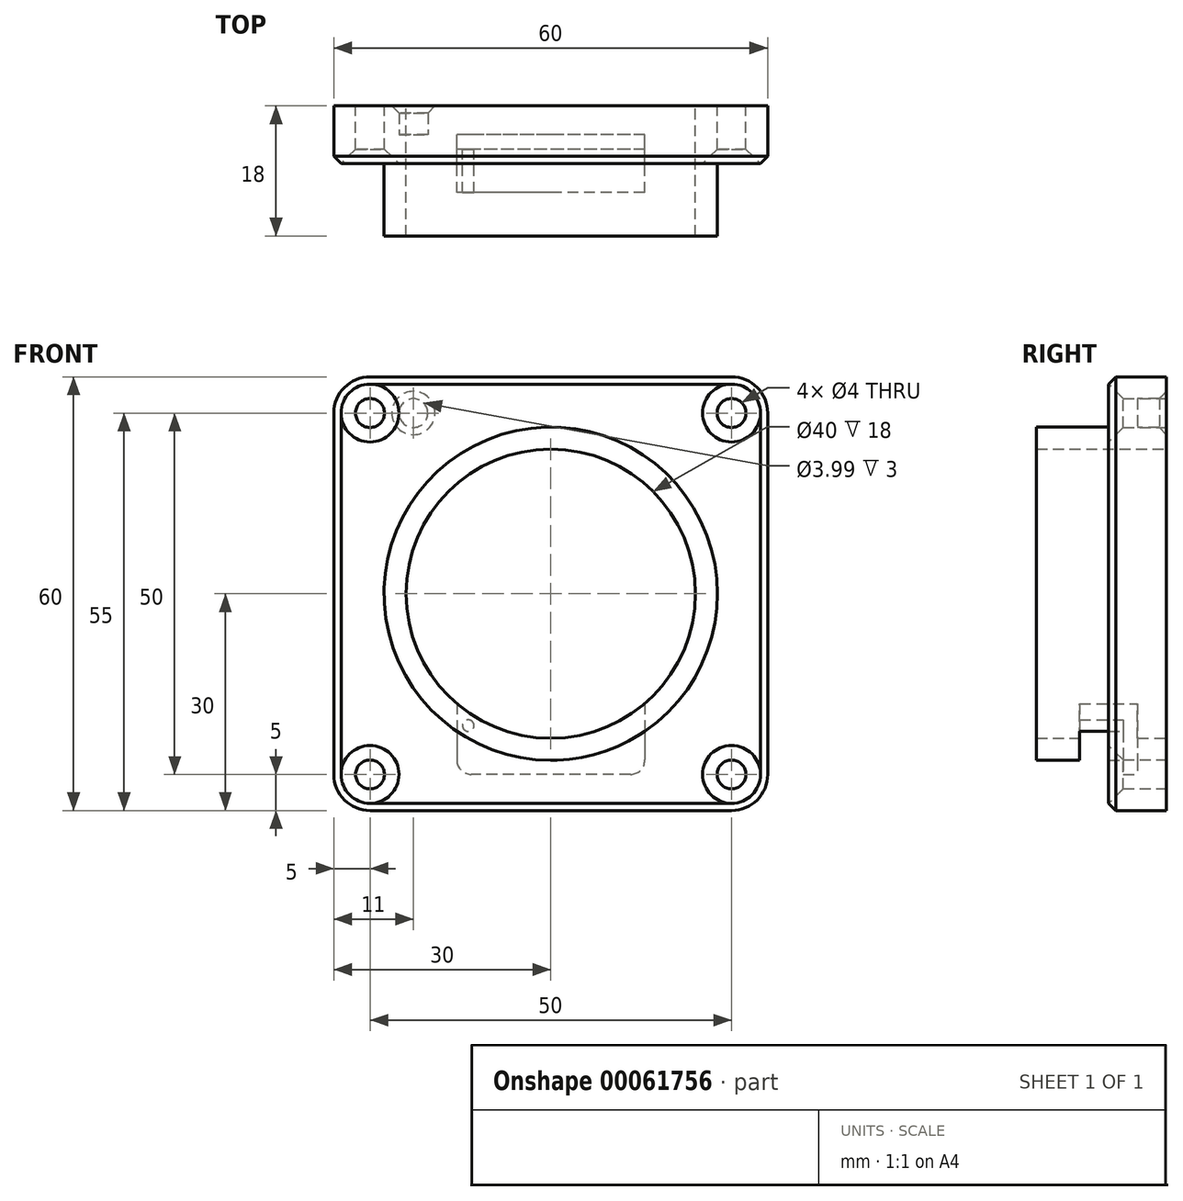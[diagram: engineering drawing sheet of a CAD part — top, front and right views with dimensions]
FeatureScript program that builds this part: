
annotation { "Feature Type Name" : "Feature", "Feature Type Description" : "" }
export const myFeature = defineFeature(function(context is Context, id is Id, definition is map)
    precondition{}
    {
        {
            var Q0;
            Q0=qCreatedBy(makeId("Front.planeOp"),FACE);
            var sketch = newSketch(context, id + "F0", { "sketchPlane" : qUnion([Q0])});
            skLineSegment(sketch, "E0.bottom", {"start": v(25, 30) * mm, "end": v(-25, 30) * mm});
            skLineSegment(sketch, "E0.top", {"start": v(25, -30) * mm, "end": v(-25, -30) * mm});
            skLineSegment(sketch, "E0.left", {"start": v(30, 25) * mm, "end": v(30, -25) * mm});
            skLineSegment(sketch, "E0.right", {"start": v(-30, 25) * mm, "end": v(-30, -25) * mm});
            skPoint(sketch, "E1", {"position": v(0, 30) * mm});
            skPoint(sketch, "E2", {"position": v(30, 0) * mm});
            skCircle(sketch, "E3", {"center": v(-25, 25) * mm, "radius": 2 * mm});
            skCircle(sketch, "E4.MirrorC", {"center": v(25, 25) * mm, "radius": 2 * mm});
            skCircle(sketch, "E5.MirrorC", {"center": v(-25, -25) * mm, "radius": 2 * mm});
            skCircle(sketch, "E6.MirrorC", {"center": v(25, -25) * mm, "radius": 2 * mm});
            skPoint(sketch, "E7.visualSharp", {"position": v(-30, 30) * mm});
            skArc(sketch, "E7.filletArc", {"start": v(-25, 30) * mm, "mid": v(-28.54, 28.54) * mm, "end": v(-30, 25) * mm});
            skPoint(sketch, "E8.visualSharp", {"position": v(30, 30) * mm});
            skArc(sketch, "E8.filletArc", {"start": v(30, 25) * mm, "mid": v(28.54, 28.54) * mm, "end": v(25, 30) * mm});
            skPoint(sketch, "E9.visualSharp", {"position": v(30, -30) * mm});
            skArc(sketch, "E9.filletArc", {"start": v(25, -30) * mm, "mid": v(28.54, -28.54) * mm, "end": v(30, -25) * mm});
            skPoint(sketch, "E10.visualSharp", {"position": v(-30, -30) * mm});
            skArc(sketch, "E10.filletArc", {"start": v(-30, -25) * mm, "mid": v(-28.54, -28.54) * mm, "end": v(-25, -30) * mm});
            skCircle(sketch, "E11", {"center": v(0, 0) * mm, "radius": 20 * mm});
            skSolve(sketch);
        }
        {
            var Q0;
            Q0=makeQuery(id+"F0.imprint","IMPRINT",FACE,{"disambiguationData":[TD([[makeQuery(id+"F0.imprint","IMPRINT",EDGE,{"derivedFrom":sQuery(id+"F0.wireOp",EDGE,"E0.bottom")}),1.0]])]});
            extrude(context, id + "F1", {"entities" : qUnion([Q0]), "depth" : 4 * mm});
        }
        {
            var Q0;
            Q0=makeQuery(id+"F1.opExtrude","CAP_FACE",FACE,{"disambiguationData":[OSD([sQuery(id+"F0.wireOp",EDGE,"E0.bottom"),sQuery(id+"F0.wireOp",EDGE,"E0.top"),sQuery(id+"F0.wireOp",EDGE,"E0.left"),sQuery(id+"F0.wireOp",EDGE,"E0.right"),sQuery(id+"F0.wireOp",EDGE,"E3"),sQuery(id+"F0.wireOp",EDGE,"E4.MirrorC"),sQuery(id+"F0.wireOp",EDGE,"E5.MirrorC"),sQuery(id+"F0.wireOp",EDGE,"E6.MirrorC"),sQuery(id+"F0.wireOp",EDGE,"E7.filletArc"),sQuery(id+"F0.wireOp",EDGE,"E8.filletArc"),sQuery(id+"F0.wireOp",EDGE,"E9.filletArc"),sQuery(id+"F0.wireOp",EDGE,"E10.filletArc"),sQuery(id+"F0.wireOp",EDGE,"74017124-3e05-427a-b8e4-af609694847d.bottom"),sQuery(id+"F0.wireOp",EDGE,"74017124-3e05-427a-b8e4-af609694847d.top"),sQuery(id+"F0.wireOp",EDGE,"74017124-3e05-427a-b8e4-af609694847d.left"),sQuery(id+"F0.wireOp",EDGE,"74017124-3e05-427a-b8e4-af609694847d.right"),sQuery(id+"F0.wireOp",EDGE,"8a5725f9-208e-47c7-ad8a-a344d27b9ad4.filletArc"),sQuery(id+"F0.wireOp",EDGE,"34e853ff-a61b-4a46-9221-9543787036cd.filletArc"),sQuery(id+"F0.wireOp",EDGE,"1b7ca9ec-e36b-44de-8ecb-2f01a231179c.filletArc"),sQuery(id+"F0.wireOp",EDGE,"5f012eeb-bb5c-4c35-9c7e-adf75f7540f9.filletArc")])],"isStart":true});
            var sketch = newSketch(context, id + "F2", { "sketchPlane" : qUnion([Q0])});
            skCircle(sketch, "E12", {"center": v(-19, 25) * mm, "radius": 2 * mm});
            skLineSegment(sketch, "E13", {"start": v(-25, 25) * mm, "end": v(25, 25) * mm, "construction": true});
            skLineSegment(sketch, "E14", {"start": v(25, 25) * mm, "end": v(25, -25) * mm, "construction": true});
            skLineSegment(sketch, "E15", {"start": v(25, -25) * mm, "end": v(-25, -25) * mm, "construction": true});
            skLineSegment(sketch, "E16", {"start": v(-25, -25) * mm, "end": v(-25, 25) * mm, "construction": true});
            skCircle(sketch, "E17.MirrorC", {"center": v(19, 25) * mm, "radius": 2 * mm});
            skCircle(sketch, "E18.MirrorC", {"center": v(19, -25) * mm, "radius": 2 * mm});
            skCircle(sketch, "E19", {"center": v(-16, -25) * mm, "radius": 2 * mm});
            skSolve(sketch);
        }
        {
            var Q0;
            Q0=makeQuery(id+"F2.imprint","IMPRINT",FACE,{"disambiguationData":[TD([[makeQuery(id+"F2.imprint","IMPRINT",EDGE,{"derivedFrom":sQuery(id+"F2.wireOp",EDGE,"E12")}),1.0]])]});
            var Q1;
            Q1=makeQuery(id+"F2.imprint","IMPRINT",FACE,{"disambiguationData":[TD([[makeQuery(id+"F2.imprint","IMPRINT",EDGE,{"derivedFrom":sQuery(id+"F2.wireOp",EDGE,"E17.MirrorC")}),-1.0]])]});
            var Q2;
            Q2=makeQuery(id+"F2.imprint","IMPRINT",FACE,{"disambiguationData":[TD([[makeQuery(id+"F2.imprint","IMPRINT",EDGE,{"derivedFrom":sQuery(id+"F2.wireOp",EDGE,"E18.MirrorC")}),1.0]])]});
            var Q3;
            Q3=makeQuery(id+"F2.imprint","IMPRINT",FACE,{"disambiguationData":[TD([[makeQuery(id+"F2.imprint","IMPRINT",EDGE,{"derivedFrom":sQuery(id+"F2.wireOp",EDGE,"E19")}),1.0]])]});
            extrude(context, id + "F3", {"entities" : qUnion([Q0, Q1, Q2, Q3]), "operationType" : NewBodyOperationType.ADD, "depth" : 4 * mm});
        }
        {
            var Q0;
            Q0=makeQuery(id+"F3.opExtrude","CAP_EDGE",EDGE,{"disambiguationData":[OSD([sQuery(id+"F2.wireOp",EDGE,"E19")])],"isStart":false});
            var Q1;
            Q1=makeQuery(id+"F3.opExtrude","CAP_EDGE",EDGE,{"disambiguationData":[OSD([sQuery(id+"F2.wireOp",EDGE,"E18.MirrorC")])],"isStart":false});
            var Q2;
            Q2=makeQuery(id+"F3.opExtrude","CAP_EDGE",EDGE,{"disambiguationData":[OSD([sQuery(id+"F2.wireOp",EDGE,"E17.MirrorC")])],"isStart":false});
            var Q3;
            Q3=makeQuery(id+"F3.opExtrude","CAP_EDGE",EDGE,{"disambiguationData":[OSD([sQuery(id+"F2.wireOp",EDGE,"E12")])],"isStart":false});
            chamfer(context, id + "F4", {"entities" : qUnion([Q0, Q1, Q2, Q3]), "width" : 1 * mm, "tangentPropagation" : true});
        }
        {
            var Q0;
            Q0=makeQuery(id+"F1.opExtrude","CAP_FACE",FACE,{"disambiguationData":[OSD([sQuery(id+"F0.wireOp",EDGE,"E0.bottom"),sQuery(id+"F0.wireOp",EDGE,"E0.top"),sQuery(id+"F0.wireOp",EDGE,"E0.left"),sQuery(id+"F0.wireOp",EDGE,"E0.right"),sQuery(id+"F0.wireOp",EDGE,"E3"),sQuery(id+"F0.wireOp",EDGE,"E4.MirrorC"),sQuery(id+"F0.wireOp",EDGE,"E5.MirrorC"),sQuery(id+"F0.wireOp",EDGE,"E6.MirrorC"),sQuery(id+"F0.wireOp",EDGE,"E7.filletArc"),sQuery(id+"F0.wireOp",EDGE,"E8.filletArc"),sQuery(id+"F0.wireOp",EDGE,"E9.filletArc"),sQuery(id+"F0.wireOp",EDGE,"E10.filletArc"),sQuery(id+"F0.wireOp",EDGE,"74017124-3e05-427a-b8e4-af609694847d.bottom"),sQuery(id+"F0.wireOp",EDGE,"74017124-3e05-427a-b8e4-af609694847d.top"),sQuery(id+"F0.wireOp",EDGE,"74017124-3e05-427a-b8e4-af609694847d.left"),sQuery(id+"F0.wireOp",EDGE,"74017124-3e05-427a-b8e4-af609694847d.right"),sQuery(id+"F0.wireOp",EDGE,"8a5725f9-208e-47c7-ad8a-a344d27b9ad4.filletArc"),sQuery(id+"F0.wireOp",EDGE,"34e853ff-a61b-4a46-9221-9543787036cd.filletArc"),sQuery(id+"F0.wireOp",EDGE,"1b7ca9ec-e36b-44de-8ecb-2f01a231179c.filletArc"),sQuery(id+"F0.wireOp",EDGE,"5f012eeb-bb5c-4c35-9c7e-adf75f7540f9.filletArc")])],"isStart":false});
            var sketch = newSketch(context, id + "F5", { "sketchPlane" : qUnion([Q0])});
            skCircle(sketch, "E20", {"center": v(0, 0) * mm, "radius": 23.05 * mm});
            skCircle(sketch, "E21", {"center": v(0, 0) * mm, "radius": 20 * mm});
            skSolve(sketch);
        }
        {
            var Q0;
            Q0=makeQuery(id+"F5.imprint","IMPRINT",FACE,{"disambiguationData":[TD([[makeQuery(id+"F5.imprint","IMPRINT",EDGE,{"derivedFrom":sQuery(id+"F5.wireOp",EDGE,"E20")}),1.0]])]});
            extrude(context, id + "F6", {"entities" : qUnion([Q0]), "operationType" : NewBodyOperationType.ADD, "depth" : 10 * mm});
        }
        {
            var Q0;
            Q0=makeQuery(id+"F1.opExtrude","CAP_FACE",FACE,{"disambiguationData":[OSD([sQuery(id+"F0.wireOp",EDGE,"E0.bottom"),sQuery(id+"F0.wireOp",EDGE,"E0.top"),sQuery(id+"F0.wireOp",EDGE,"E0.left"),sQuery(id+"F0.wireOp",EDGE,"E0.right"),sQuery(id+"F0.wireOp",EDGE,"E3"),sQuery(id+"F0.wireOp",EDGE,"E4.MirrorC"),sQuery(id+"F0.wireOp",EDGE,"E5.MirrorC"),sQuery(id+"F0.wireOp",EDGE,"E6.MirrorC"),sQuery(id+"F0.wireOp",EDGE,"E7.filletArc"),sQuery(id+"F0.wireOp",EDGE,"E8.filletArc"),sQuery(id+"F0.wireOp",EDGE,"E9.filletArc"),sQuery(id+"F0.wireOp",EDGE,"E10.filletArc"),sQuery(id+"F0.wireOp",EDGE,"E11")])],"isStart":true});
            var sketch = newSketch(context, id + "F7", { "sketchPlane" : qUnion([Q0])});
            skLineSegment(sketch, "E22.bottom", {"start": v(-13, -10) * mm, "end": v(13, -10) * mm});
            skLineSegment(sketch, "E22.top", {"start": v(-11, -25) * mm, "end": v(11, -25) * mm});
            skLineSegment(sketch, "E22.left", {"start": v(-13, -10) * mm, "end": v(-13, -23) * mm});
            skLineSegment(sketch, "E22.right", {"start": v(13, -10) * mm, "end": v(13, -23) * mm});
            skArc(sketch, "E23.0.0", {"start": v(-25, 30) * mm, "mid": v(-28.54, 28.54) * mm, "end": v(-30, 25) * mm});
            skLineSegment(sketch, "E23.0.1", {"start": v(-30, 25) * mm, "end": v(-30, -25) * mm});
            skArc(sketch, "E23.0.2", {"start": v(-30, -25) * mm, "mid": v(-28.54, -28.54) * mm, "end": v(-25, -30) * mm});
            skLineSegment(sketch, "E23.0.3", {"start": v(-25, -30) * mm, "end": v(25, -30) * mm});
            skArc(sketch, "E23.0.4", {"start": v(25, -30) * mm, "mid": v(28.54, -28.54) * mm, "end": v(30, -25) * mm});
            skLineSegment(sketch, "E23.0.5", {"start": v(30, -25) * mm, "end": v(30, 25) * mm});
            skArc(sketch, "E23.0.6", {"start": v(30, 25) * mm, "mid": v(28.54, 28.54) * mm, "end": v(25, 30) * mm});
            skLineSegment(sketch, "E23.0.7", {"start": v(25, 30) * mm, "end": v(-25, 30) * mm});
            skLineSegment(sketch, "E24", {"start": v(-25, -25) * mm, "end": v(25, -25) * mm, "construction": true});
            skPoint(sketch, "E25", {"position": v(0, -10) * mm});
            skPoint(sketch, "E26.visualSharp", {"position": v(-13, -25) * mm});
            skArc(sketch, "E26.filletArc", {"start": v(-13, -23) * mm, "mid": v(-12.41, -24.41) * mm, "end": v(-11, -25) * mm});
            skPoint(sketch, "E27.visualSharp", {"position": v(13, -25) * mm});
            skArc(sketch, "E27.filletArc", {"start": v(11, -25) * mm, "mid": v(12.41, -24.41) * mm, "end": v(13, -23) * mm});
            skSolve(sketch);
        }
        {
            var Q0;
            {var subQ0=sQuery(id+"F7.wireOp",EDGE,"E22.top");Q0=makeQuery(id+"F7.imprint","IMPRINT",FACE,{"disambiguationData":[TD([[makeQuery(id+"F7.imprint","IMPRINT",EDGE,{"derivedFrom":subQ0}),1.0]])]});}
            extrude(context, id + "F8", {"entities" : qUnion([Q0]), "operationType" : NewBodyOperationType.REMOVE, "oppositeDirection" : true, "depth" : 2 * mm});
        }
        {
            var Q0;
            Q0=makeQuery(id+"F8.boolean.opBoolean","COPY",FACE,{"derivedFrom":makeQuery(id+"F8.opExtrude","CAP_FACE",FACE,{"disambiguationData":[OSD([sQuery(id+"F0.wireOp",EDGE,"E11"),sQuery(id+"F7.wireOp",EDGE,"E22.top"),sQuery(id+"F7.wireOp",EDGE,"E22.left"),sQuery(id+"F7.wireOp",EDGE,"E22.right"),sQuery(id+"F7.wireOp",EDGE,"E26.filletArc"),sQuery(id+"F7.wireOp",EDGE,"E27.filletArc")])],"isStart":false})});
            var sketch = newSketch(context, id + "F9", { "sketchPlane" : qUnion([Q0])});
            skCircle(sketch, "E28", {"center": v(-11.4, -18.25) * mm, "radius": 0.8 * mm});
            skCircle(sketch, "E29.0.0", {"center": v(0, 0) * mm, "radius": 23.05 * mm});
            skLineSegment(sketch, "E30", {"start": v(-10.6, -16.96) * mm, "end": v(-12.21, -19.55) * mm, "construction": true});
            skCircle(sketch, "E31.MirrorC", {"center": v(11.4, -18.25) * mm, "radius": 0.8 * mm});
            skSolve(sketch);
        }
        {
            var Q0;
            Q0=makeQuery(id+"F9.imprint","IMPRINT",FACE,{"disambiguationData":[TD([[makeQuery(id+"F9.imprint","IMPRINT",EDGE,{"derivedFrom":sQuery(id+"F9.wireOp",EDGE,"E28")}),1.0]])]});
            var Q1;
            Q1=makeQuery(id+"F9.imprint","IMPRINT",FACE,{"disambiguationData":[TD([[makeQuery(id+"F9.imprint","IMPRINT",EDGE,{"derivedFrom":sQuery(id+"F9.wireOp",EDGE,"E31.MirrorC")}),-1.0]])]});
            extrude(context, id + "F10", {"entities" : qUnion([Q0, Q1]), "operationType" : NewBodyOperationType.REMOVE, "oppositeDirection" : true, "depth" : 6 * mm});
        }
        {
            var Q0;
            Q0=makeQuery(id+"F1.opExtrude","CAP_EDGE",EDGE,{"disambiguationData":[OSD([sQuery(id+"F0.wireOp",EDGE,"E4.MirrorC")])],"isStart":false});
            var Q1;
            Q1=makeQuery(id+"F1.opExtrude","CAP_EDGE",EDGE,{"disambiguationData":[OSD([sQuery(id+"F0.wireOp",EDGE,"E3")])],"isStart":false});
            var Q2;
            Q2=makeQuery(id+"F1.opExtrude","CAP_EDGE",EDGE,{"disambiguationData":[OSD([sQuery(id+"F0.wireOp",EDGE,"E5.MirrorC")])],"isStart":false});
            var Q3;
            Q3=makeQuery(id+"F1.opExtrude","CAP_EDGE",EDGE,{"disambiguationData":[OSD([sQuery(id+"F0.wireOp",EDGE,"E6.MirrorC")])],"isStart":false});
            chamfer(context, id + "F11", {"entities" : qUnion([Q0, Q1, Q2, Q3]), "width" : 2 * mm, "tangentPropagation" : true});
        }
        {
            var Q0;
            Q0=makeQuery(id+"F1.opExtrude","CAP_EDGE",EDGE,{"disambiguationData":[OSD([sQuery(id+"F0.wireOp",EDGE,"E0.left")])],"isStart":false});
            var Q1;
            Q1=makeQuery(id+"F1.opExtrude","CAP_EDGE",EDGE,{"disambiguationData":[OSD([sQuery(id+"F0.wireOp",EDGE,"E8.filletArc")])],"isStart":false});
            var Q2;
            Q2=makeQuery(id+"F1.opExtrude","CAP_EDGE",EDGE,{"disambiguationData":[OSD([sQuery(id+"F0.wireOp",EDGE,"E0.bottom")])],"isStart":false});
            var Q3;
            Q3=makeQuery(id+"F1.opExtrude","CAP_EDGE",EDGE,{"disambiguationData":[OSD([sQuery(id+"F0.wireOp",EDGE,"E7.filletArc")])],"isStart":false});
            var Q4;
            Q4=makeQuery(id+"F1.opExtrude","CAP_EDGE",EDGE,{"disambiguationData":[OSD([sQuery(id+"F0.wireOp",EDGE,"E0.right")])],"isStart":false});
            var Q5;
            Q5=makeQuery(id+"F1.opExtrude","CAP_EDGE",EDGE,{"disambiguationData":[OSD([sQuery(id+"F0.wireOp",EDGE,"E10.filletArc")])],"isStart":false});
            var Q6;
            Q6=makeQuery(id+"F1.opExtrude","CAP_EDGE",EDGE,{"disambiguationData":[OSD([sQuery(id+"F0.wireOp",EDGE,"E0.top")])],"isStart":false});
            var Q7;
            Q7=makeQuery(id+"F1.opExtrude","CAP_EDGE",EDGE,{"disambiguationData":[OSD([sQuery(id+"F0.wireOp",EDGE,"E9.filletArc")])],"isStart":false});
            chamfer(context, id + "F12", {"entities" : qUnion([Q0, Q1, Q2, Q3, Q4, Q5, Q6, Q7]), "width" : 1 * mm, "tangentPropagation" : true});
        }
    });
